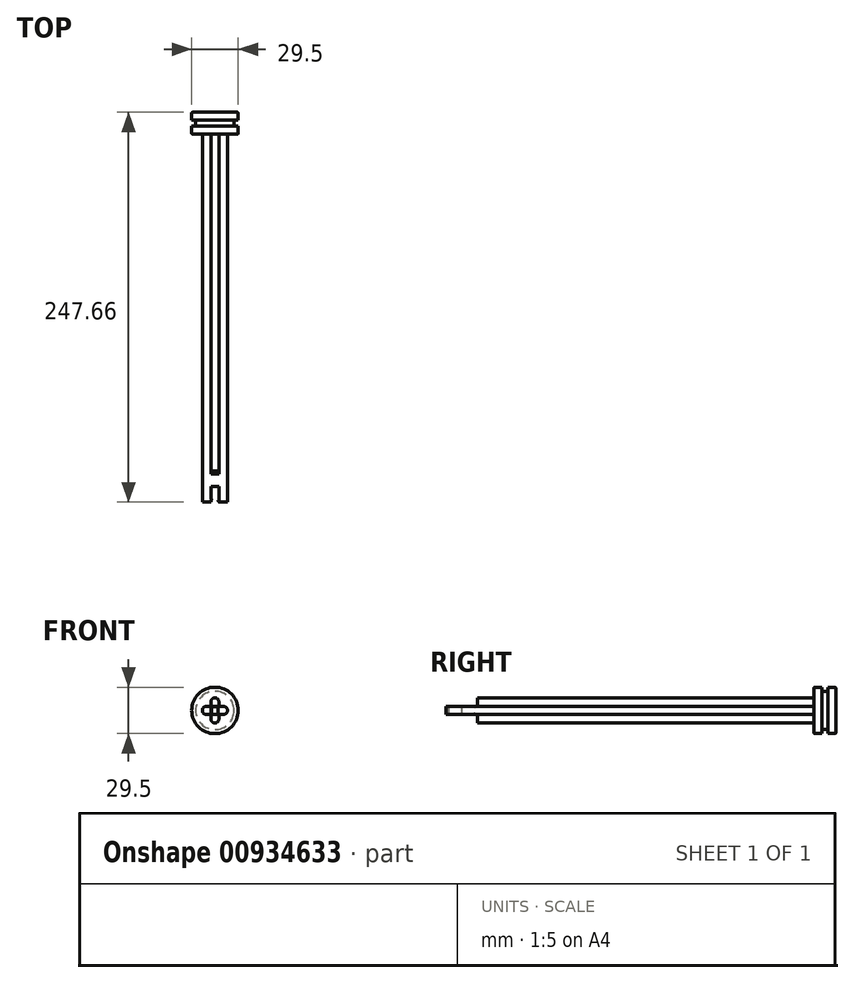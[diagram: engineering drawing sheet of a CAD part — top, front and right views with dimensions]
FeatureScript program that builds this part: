
annotation { "Feature Type Name" : "Feature", "Feature Type Description" : "" }
export const myFeature = defineFeature(function(context is Context, id is Id, definition is map)
    precondition{}
    {
        {
            var Q0;
            Q0=qCreatedBy(makeId("Front.planeOp"),FACE);
            var sketch = newSketch(context, id + "F0", { "sketchPlane" : qUnion([Q0])});
            skLineSegment(sketch, "E0.bottom", {"start": v(2.5, 8) * mm, "end": v(-2.5, 8) * mm});
            skLineSegment(sketch, "E0.top", {"start": v(2.5, -8) * mm, "end": v(-2.5, -8) * mm});
            skLineSegment(sketch, "E0.left", {"start": v(2.5, 8) * mm, "end": v(2.5, -8) * mm});
            skLineSegment(sketch, "E0.right", {"start": v(-2.5, 8) * mm, "end": v(-2.5, -8) * mm});
            skPoint(sketch, "E0.middle", {"position": v(0, 0) * mm});
            skLineSegment(sketch, "E1.bottom", {"start": v(-8, -2.5) * mm, "end": v(8, -2.5) * mm});
            skLineSegment(sketch, "E1.top", {"start": v(-8, 2.5) * mm, "end": v(8, 2.5) * mm});
            skLineSegment(sketch, "E1.left", {"start": v(-8, -2.5) * mm, "end": v(-8, 2.5) * mm});
            skLineSegment(sketch, "E1.right", {"start": v(8, -2.5) * mm, "end": v(8, 2.5) * mm});
            skSolve(sketch);
        }
        {
            var Q0;
            {var subQ5=sQuery(id+"F0.wireOp",EDGE,"E1.left");Q0=makeQuery(id+"F0.imprint","IMPRINT",FACE,{"disambiguationData":[TD([[makeQuery(id+"F0.imprint","IMPRINT",EDGE,{"derivedFrom":subQ5}),-1.0]])]});}
            var Q1;
            {var subQ0=sQuery(id+"F0.wireOp",EDGE,"E1.top");var subQ1=sQuery(id+"F0.wireOp",EDGE,"E0.left");var subQ2=makeQuery(id+"F0.imprint","INTERSECT",VERTEX,{"derivedFrom":[subQ1,subQ0]});Q1=makeQuery(id+"F0.imprint","IMPRINT",FACE,{"disambiguationData":[TD([[makeQuery(id+"F0.imprint","IMPRINT",EDGE,{"disambiguationData":[TD([[subQ2,-1.0]])],"derivedFrom":subQ1}),-1.0]])]});}
            var Q2;
            {var subQ5=sQuery(id+"F0.wireOp",EDGE,"E1.right");Q2=makeQuery(id+"F0.imprint","IMPRINT",FACE,{"disambiguationData":[TD([[makeQuery(id+"F0.imprint","IMPRINT",EDGE,{"derivedFrom":subQ5}),1.0]])]});}
            var Q3;
            {var subQ0=sQuery(id+"F0.wireOp",EDGE,"E0.top");Q3=makeQuery(id+"F0.imprint","IMPRINT",FACE,{"disambiguationData":[TD([[makeQuery(id+"F0.imprint","IMPRINT",EDGE,{"derivedFrom":subQ0}),-1.0]])]});}
            var Q4;
            {var subQ0=sQuery(id+"F0.wireOp",EDGE,"E0.bottom");Q4=makeQuery(id+"F0.imprint","IMPRINT",FACE,{"disambiguationData":[TD([[makeQuery(id+"F0.imprint","IMPRINT",EDGE,{"derivedFrom":subQ0}),1.0]])]});}
            extrude(context, id + "F1", {"entities" : qUnion([Q0, Q1, Q2, Q3, Q4]), "depth" : 233.86 * mm, "offsetDistance" : 25.4 * mm});
        }
        {
            var Q0;
            Q0=makeQuery(id+"F1.opExtrude","SWEPT_EDGE",EDGE,{"disambiguationData":[OSD([sQuery(id+"F0.wireOp",EDGE,"E0.bottom"),sQuery(id+"F0.wireOp",EDGE,"E0.right")])]});
            var Q1;
            Q1=makeQuery(id+"F1.opExtrude","SWEPT_EDGE",EDGE,{"disambiguationData":[OSD([sQuery(id+"F0.wireOp",EDGE,"E0.bottom"),sQuery(id+"F0.wireOp",EDGE,"E0.left")])]});
            var Q2;
            Q2=makeQuery(id+"F1.opExtrude","SWEPT_EDGE",EDGE,{"disambiguationData":[OSD([sQuery(id+"F0.wireOp",EDGE,"E1.top"),sQuery(id+"F0.wireOp",EDGE,"E1.left")])]});
            var Q3;
            Q3=makeQuery(id+"F1.opExtrude","SWEPT_EDGE",EDGE,{"disambiguationData":[OSD([sQuery(id+"F0.wireOp",EDGE,"E1.bottom"),sQuery(id+"F0.wireOp",EDGE,"E1.left")])]});
            var Q4;
            Q4=makeQuery(id+"F1.opExtrude","SWEPT_EDGE",EDGE,{"disambiguationData":[OSD([sQuery(id+"F0.wireOp",EDGE,"E0.top"),sQuery(id+"F0.wireOp",EDGE,"E0.right")])]});
            var Q5;
            Q5=makeQuery(id+"F1.opExtrude","SWEPT_EDGE",EDGE,{"disambiguationData":[OSD([sQuery(id+"F0.wireOp",EDGE,"E0.top"),sQuery(id+"F0.wireOp",EDGE,"E0.left")])]});
            var Q6;
            Q6=makeQuery(id+"F1.opExtrude","SWEPT_EDGE",EDGE,{"disambiguationData":[OSD([sQuery(id+"F0.wireOp",EDGE,"E1.bottom"),sQuery(id+"F0.wireOp",EDGE,"E1.right")])]});
            var Q7;
            Q7=makeQuery(id+"F1.opExtrude","SWEPT_EDGE",EDGE,{"disambiguationData":[OSD([sQuery(id+"F0.wireOp",EDGE,"E1.top"),sQuery(id+"F0.wireOp",EDGE,"E1.right")])]});
            fillet(context, id + "F2", {"entities" : qUnion([Q0, Q1, Q2, Q3, Q4, Q5, Q6, Q7]), "radius" : 2.5 * mm, "tangentPropagation" : true, "allowEdgeOverflow" : false});
        }
        {
            var Q0;
            Q0=qCreatedBy(makeId("Front.planeOp"),FACE);
            var sketch = newSketch(context, id + "F3", { "sketchPlane" : qUnion([Q0])});
            skCircle(sketch, "E2", {"center": v(0, 0) * mm, "radius": 14.75 * mm});
            skCircle(sketch, "E3", {"center": v(0, 0) * mm, "radius": 12.2 * mm});
            skSolve(sketch);
        }
        {
            var Q0;
            Q0=makeQuery(id+"F3.imprint","IMPRINT",FACE,{"disambiguationData":[TD([[makeQuery(id+"F3.imprint","IMPRINT",EDGE,{"derivedFrom":sQuery(id+"F3.wireOp",EDGE,"E2")}),1.0]])]});
            var Q1;
            Q1=makeQuery(id+"F3.imprint","IMPRINT",FACE,{"disambiguationData":[TD([[makeQuery(id+"F3.imprint","IMPRINT",EDGE,{"derivedFrom":sQuery(id+"F3.wireOp",EDGE,"E3")}),1.0]])]});
            extrude(context, id + "F4", {"entities" : qUnion([Q0, Q1]), "operationType" : NewBodyOperationType.ADD, "oppositeDirection" : true, "depth" : 13.8 * mm, "offsetDistance" : 25.4 * mm});
        }
        {
            var Q0;
            {var subQ0=sQuery(id+"F0.wireOp",EDGE,"E0.right");Q0=makeQuery(id+"F1.opExtrude","CAP_EDGE",EDGE,{"disambiguationData":[OSD([subQ0]),TDD([makeQuery(id+"F0.imprint","IMPRINT",EDGE,{"disambiguationData":[TD([[makeQuery(id+"F0.imprint","INTERSECT",VERTEX,{"derivedFrom":[sQuery(id+"F0.wireOp",EDGE,"E0.bottom"),subQ0]}),-1.0]])],"derivedFrom":subQ0})])],"isStart":true});}
            var Q1;
            Q1=makeQuery(id+"F4.opExtrude","CAP_FACE",FACE,{"disambiguationData":[OSD([sQuery(id+"F3.wireOp",EDGE,"E2")])],"isStart":true});
            var Q2;
            Q2=makeQuery(id+"F4.opExtrude","CAP_EDGE",EDGE,{"disambiguationData":[OSD([sQuery(id+"F3.wireOp",EDGE,"E2")])],"isStart":false});
            fillet(context, id + "F5", {"entities" : qUnion([Q0, Q1, Q2]), "radius" : 0.5 * mm, "tangentPropagation" : true, "allowEdgeOverflow" : false});
        }
        {
            var Q0;
            Q0=qCreatedBy(makeId("Right.planeOp"),FACE);
            var sketch = newSketch(context, id + "F6", { "sketchPlane" : qUnion([Q0])});
            skLineSegment(sketch, "E4.bottom", {"start": v(5, 22.2) * mm, "end": v(8.8, 22.2) * mm});
            skLineSegment(sketch, "E4.top", {"start": v(5, 12.2) * mm, "end": v(8.8, 12.2) * mm});
            skLineSegment(sketch, "E4.left", {"start": v(5, 22.2) * mm, "end": v(5, 12.2) * mm});
            skLineSegment(sketch, "E4.right", {"start": v(8.8, 22.2) * mm, "end": v(8.8, 12.2) * mm});
            skLineSegment(sketch, "E5", {"start": v(0, 0) * mm, "end": v(33.95, 0) * mm});
            skSolve(sketch);
        }
        {
            var Q0;
            Q0=makeQuery(id+"F6.imprint","IMPRINT",FACE,{"disambiguationData":[TD([[makeQuery(id+"F6.imprint","IMPRINT",EDGE,{"derivedFrom":sQuery(id+"F6.wireOp",EDGE,"E4.bottom")}),-1.0]])]});
            var Q1;
            Q1=sQuery(id+"F6.wireOp",EDGE,"E5");
            revolve(context, id + "F7", {"operationType" : NewBodyOperationType.REMOVE, "surfaceOperationType" : NewSurfaceOperationType.NEW, "entities" : qUnion([Q0]), "axis" : qUnion([Q1]), "revolveType" : RevolveType.FULL, "oppositeDirection" : true});
        }
        {
            var Q0;
            Q0=makeQuery(id+"F1.opExtrude","CAP_FACE",FACE,{"disambiguationData":[OSD([sQuery(id+"F0.wireOp",EDGE,"E0.bottom"),sQuery(id+"F0.wireOp",EDGE,"E0.top"),sQuery(id+"F0.wireOp",EDGE,"E0.left"),sQuery(id+"F0.wireOp",EDGE,"E0.right"),sQuery(id+"F0.wireOp",EDGE,"E1.bottom"),sQuery(id+"F0.wireOp",EDGE,"E1.top"),sQuery(id+"F0.wireOp",EDGE,"E1.left"),sQuery(id+"F0.wireOp",EDGE,"E1.right")])],"isStart":false});
            var sketch = newSketch(context, id + "F8", { "sketchPlane" : qUnion([Q0])});
            skLineSegment(sketch, "E6.bottom", {"start": v(2.5, 10) * mm, "end": v(-2.5, 10) * mm});
            skLineSegment(sketch, "E6.top", {"start": v(2.5, -10) * mm, "end": v(-2.5, -10) * mm});
            skLineSegment(sketch, "E6.left", {"start": v(2.5, 10) * mm, "end": v(2.5, -10) * mm});
            skLineSegment(sketch, "E6.right", {"start": v(-2.5, 10) * mm, "end": v(-2.5, -10) * mm});
            skPoint(sketch, "E6.middle", {"position": v(0, 0) * mm});
            skSolve(sketch);
        }
        {
            var Q0;
            {var subQ1=sQuery(id+"F0.wireOp",EDGE,"E1.top");var subQ2=sQuery(id+"F0.wireOp",EDGE,"E1.bottom");var subQ3=sQuery(id+"F0.wireOp",EDGE,"E0.right");var subQ4=sQuery(id+"F0.wireOp",EDGE,"E0.left");var subQ5=sQuery(id+"F0.wireOp",EDGE,"E0.top");var subQ6=sQuery(id+"F0.wireOp",EDGE,"E0.bottom");var subQ7=makeQuery(id+"F1.opExtrude","CAP_FACE",FACE,{"disambiguationData":[OSD([subQ6,subQ5,subQ4,subQ3,subQ2,subQ1,sQuery(id+"F0.wireOp",EDGE,"E1.left"),sQuery(id+"F0.wireOp",EDGE,"E1.right")])],"isStart":false});var subQ11=makeQuery(id+"F2.opFillet","BLEND_EDGE",EDGE,{"blendedFrom":[makeQuery(id+"F1.opExtrude","SWEPT_EDGE",EDGE,{"disambiguationData":[OSD([subQ6,subQ4])]}),subQ7],"blendedInto":[subQ7]});Q0=makeQuery(id+"F8.imprint","IMPRINT",FACE,{"disambiguationData":[TD([[makeQuery(id+"F8.imprint","IMPRINT",EDGE,{"derivedFrom":subQ11}),1.0]])]});}
            extrude(context, id + "F9", {"entities" : qUnion([Q0]), "operationType" : NewBodyOperationType.REMOVE, "oppositeDirection" : true, "depth" : 10 * mm, "offsetDistance" : 25 * mm});
        }
        {
            var Q0;
            Q0=makeQuery(id+"F9.boolean.opBoolean","COPY",FACE,{"derivedFrom":makeQuery(id+"F9.opExtrude","CAP_FACE",FACE,{"disambiguationData":[OSD([sQuery(id+"F0.wireOp",EDGE,"E0.bottom"),sQuery(id+"F0.wireOp",EDGE,"E0.top"),sQuery(id+"F0.wireOp",EDGE,"E0.left"),sQuery(id+"F0.wireOp",EDGE,"E0.right"),sQuery(id+"F0.wireOp",EDGE,"E1.bottom"),sQuery(id+"F0.wireOp",EDGE,"E1.top"),sQuery(id+"F0.wireOp",EDGE,"E1.left"),sQuery(id+"F0.wireOp",EDGE,"E1.right"),sQuery(id+"F8.wireOp",EDGE,"E6.left"),sQuery(id+"F8.wireOp",EDGE,"E6.right")])],"isStart":false})});
            var sketch = newSketch(context, id + "F10", { "sketchPlane" : qUnion([Q0])});
            skLineSegment(sketch, "E7.bottom", {"start": v(0, 8) * mm, "end": v(2.5, 8) * mm});
            skLineSegment(sketch, "E7.top", {"start": v(0, 2.5) * mm, "end": v(2.5, 2.5) * mm});
            skLineSegment(sketch, "E7.left", {"start": v(0, 8) * mm, "end": v(0, 2.5) * mm});
            skLineSegment(sketch, "E7.right", {"start": v(2.5, 8) * mm, "end": v(2.5, 2.5) * mm});
            skLineSegment(sketch, "E8.MirrorCS", {"start": v(0, 8) * mm, "end": v(-2.5, 8) * mm});
            skLineSegment(sketch, "E9.MirrorCS", {"start": v(-2.5, 8) * mm, "end": v(-2.5, 2.5) * mm});
            skLineSegment(sketch, "E10.MirrorCS", {"start": v(0, 2.5) * mm, "end": v(-2.5, 2.5) * mm});
            skLineSegment(sketch, "E11.bottom", {"start": v(-2.5, 8) * mm, "end": v(2.5, 8) * mm});
            skLineSegment(sketch, "E11.top", {"start": v(-2.5, 2.5) * mm, "end": v(2.5, 2.5) * mm});
            skLineSegment(sketch, "E12.MirrorCS", {"start": v(-2.5, -8) * mm, "end": v(-2.5, -2.5) * mm});
            skLineSegment(sketch, "E13.MirrorCS", {"start": v(-2.5, -8) * mm, "end": v(2.5, -8) * mm});
            skLineSegment(sketch, "E14.MirrorCS", {"start": v(2.5, -8) * mm, "end": v(2.5, -2.5) * mm});
            skLineSegment(sketch, "E15.MirrorCS", {"start": v(-2.5, -2.5) * mm, "end": v(2.5, -2.5) * mm});
            skSolve(sketch);
        }
        {
            var Q0;
            {var subQ15=sQuery(id+"F10.wireOp",EDGE,"E7.left");Q0=makeQuery(id+"F10.imprint","IMPRINT",FACE,{"disambiguationData":[TD([[makeQuery(id+"F10.imprint","IMPRINT",EDGE,{"derivedFrom":subQ15}),-1.0]])]});}
            var Q1;
            {var subQ13=sQuery(id+"F10.wireOp",EDGE,"E7.left");Q1=makeQuery(id+"F10.imprint","IMPRINT",FACE,{"disambiguationData":[TD([[makeQuery(id+"F10.imprint","IMPRINT",EDGE,{"derivedFrom":subQ13}),1.0]])]});}
            var Q2;
            {var subQ16=sQuery(id+"F10.wireOp",EDGE,"E15.MirrorCS");Q2=makeQuery(id+"F10.imprint","IMPRINT",FACE,{"disambiguationData":[TD([[makeQuery(id+"F10.imprint","IMPRINT",EDGE,{"derivedFrom":subQ16}),-1.0]])]});}
            extrude(context, id + "F11", {"entities" : qUnion([Q0, Q1, Q2]), "operationType" : NewBodyOperationType.REMOVE, "oppositeDirection" : true, "depth" : 10 * mm, "offsetDistance" : 25 * mm});
        }
        {
            var Q0;
            {var subQ0=sQuery(id+"F0.wireOp",EDGE,"E1.top");Q0=makeQuery(id+"F11.boolean.opBoolean","MERGE",FACE,{"derivedFrom":[makeQuery(id+"F1.opExtrude","SWEPT_FACE",FACE,{"disambiguationData":[OSD([subQ0]),TDD([makeQuery(id+"F0.imprint","IMPRINT",EDGE,{"disambiguationData":[TD([[makeQuery(id+"F0.imprint","INTERSECT",VERTEX,{"derivedFrom":[subQ0,sQuery(id+"F0.wireOp",EDGE,"E1.left")]}),-1.0]])],"derivedFrom":subQ0})])]}),makeQuery(id+"F1.opExtrude","SWEPT_FACE",FACE,{"disambiguationData":[OSD([subQ0]),TDD([makeQuery(id+"F0.imprint","IMPRINT",EDGE,{"disambiguationData":[TD([[makeQuery(id+"F0.imprint","INTERSECT",VERTEX,{"derivedFrom":[subQ0,sQuery(id+"F0.wireOp",EDGE,"E1.right")]}),1.0]])],"derivedFrom":subQ0})])]})],"fromTools":[makeQuery(id+"F11.opExtrude","SWEPT_FACE",FACE,{"disambiguationData":[OSD([sQuery(id+"F10.wireOp",EDGE,"E11.top")])]})]});}
            var sketch = newSketch(context, id + "F12", { "sketchPlane" : qUnion([Q0])});
            skLineSegment(sketch, "E16", {"start": v(2.5, -233.86) * mm, "end": v(2, -232.36) * mm});
            skLineSegment(sketch, "E17", {"start": v(2, -232.36) * mm, "end": v(2.5, -232.36) * mm});
            skLineSegment(sketch, "E18.bottom", {"start": v(2.5, -232.36) * mm, "end": v(2, -232.36) * mm});
            skLineSegment(sketch, "E18.top", {"start": v(2.5, -231.86) * mm, "end": v(2, -231.86) * mm});
            skLineSegment(sketch, "E18.left", {"start": v(2.5, -232.36) * mm, "end": v(2.5, -231.86) * mm});
            skLineSegment(sketch, "E18.right", {"start": v(2, -232.36) * mm, "end": v(2, -231.86) * mm});
            skLineSegment(sketch, "E19.bottom", {"start": v(-2.5, -233.86) * mm, "end": v(2.5, -233.86) * mm, "construction": true});
            skLineSegment(sketch, "E19.top", {"start": v(-2.5, -221.37) * mm, "end": v(2.5, -221.37) * mm, "construction": true});
            skLineSegment(sketch, "E19.left", {"start": v(-2.5, -233.86) * mm, "end": v(-2.5, -221.37) * mm, "construction": true});
            skLineSegment(sketch, "E19.right", {"start": v(2.5, -233.86) * mm, "end": v(2.5, -221.37) * mm, "construction": true});
            skLineSegment(sketch, "E20", {"start": v(0, -224.68) * mm, "end": v(0, -221.37) * mm, "construction": true});
            skPoint(sketch, "E20.startSnap0", {"position": v(0, -221.37) * mm});
            skLineSegment(sketch, "E21.MirrorCS", {"start": v(-2, -232.36) * mm, "end": v(-2.5, -232.36) * mm});
            skLineSegment(sketch, "E22.MirrorCS", {"start": v(-2.5, -232.36) * mm, "end": v(-2.5, -231.86) * mm});
            skLineSegment(sketch, "E23.MirrorCS", {"start": v(-2.5, -232.36) * mm, "end": v(-2, -232.36) * mm});
            skLineSegment(sketch, "E24.MirrorCS", {"start": v(-2, -232.36) * mm, "end": v(-2, -231.86) * mm});
            skLineSegment(sketch, "E25.MirrorCS", {"start": v(-2.5, -233.86) * mm, "end": v(-2, -232.36) * mm});
            skLineSegment(sketch, "E26.MirrorCS", {"start": v(-2.5, -231.86) * mm, "end": v(-2, -231.86) * mm});
            skSolve(sketch);
        }
        {
            var Q0;
            Q0=makeQuery(id+"F12.imprint","IMPRINT",FACE,{"disambiguationData":[TD([[makeQuery(id+"F12.imprint","IMPRINT",EDGE,{"derivedFrom":sQuery(id+"F12.wireOp",EDGE,"E22.MirrorCS")}),-1.0]])]});
            var Q1;
            {var subQ0=sQuery(id+"F12.wireOp",EDGE,"E23.MirrorCS");Q1=makeQuery(id+"F12.imprint","IMPRINT",FACE,{"disambiguationData":[TD([[makeQuery(id+"F12.imprint","IMPRINT",EDGE,{"derivedFrom":subQ0}),-1.0]])]});}
            var Q2;
            Q2=makeQuery(id+"F12.imprint","IMPRINT",FACE,{"disambiguationData":[TD([[makeQuery(id+"F12.imprint","IMPRINT",EDGE,{"derivedFrom":sQuery(id+"F12.wireOp",EDGE,"E18.bottom")}),-1.0]])]});
            var Q3;
            {var subQ0=sQuery(id+"F12.wireOp",EDGE,"E16");Q3=makeQuery(id+"F12.imprint","IMPRINT",FACE,{"disambiguationData":[TD([[makeQuery(id+"F12.imprint","IMPRINT",EDGE,{"derivedFrom":subQ0}),-1.0]])]});}
            extrude(context, id + "F13", {"entities" : qUnion([Q0, Q1, Q2, Q3]), "operationType" : NewBodyOperationType.ADD, "oppositeDirection" : true, "depth" : 5 * mm, "offsetDistance" : 25 * mm});
        }
        {
            var Q0;
            Q0=makeQuery(id+"F13.boolean.opBoolean","MERGE",EDGE,{"derivedFrom":[makeQuery(id+"F9.boolean.opBoolean","COPY",EDGE,{"derivedFrom":makeQuery(id+"F9.opExtrude","CAP_EDGE",EDGE,{"disambiguationData":[OSD([sQuery(id+"F8.wireOp",EDGE,"E6.right")])],"isStart":true})}),makeQuery(id+"F13.opExtrude","SWEPT_EDGE",EDGE,{"disambiguationData":[OSD([sQuery(id+"F0.wireOp",EDGE,"E0.right"),sQuery(id+"F0.wireOp",EDGE,"E1.top"),sQuery(id+"F12.wireOp",EDGE,"E25.MirrorCS")])]})]});
            var Q1;
            Q1=makeQuery(id+"F13.boolean.opBoolean","MERGE",EDGE,{"derivedFrom":[makeQuery(id+"F9.boolean.opBoolean","COPY",EDGE,{"derivedFrom":makeQuery(id+"F9.opExtrude","CAP_EDGE",EDGE,{"disambiguationData":[OSD([sQuery(id+"F8.wireOp",EDGE,"E6.left")])],"isStart":true})}),makeQuery(id+"F13.opExtrude","SWEPT_EDGE",EDGE,{"disambiguationData":[OSD([sQuery(id+"F0.wireOp",EDGE,"E0.left"),sQuery(id+"F0.wireOp",EDGE,"E1.top"),sQuery(id+"F12.wireOp",EDGE,"E16")])]})]});
            fillet(context, id + "F14", {"entities" : qUnion([Q0, Q1]), "radius" : .5 * mm, "tangentPropagation" : true, "allowEdgeOverflow" : false});
        }
        {
            var Q0;
            {var subQ0=sQuery(id+"F0.wireOp",EDGE,"E0.left");Q0=makeQuery(id+"F1.opExtrude","SWEPT_FACE",FACE,{"disambiguationData":[OSD([subQ0]),TDD([makeQuery(id+"F0.imprint","IMPRINT",EDGE,{"disambiguationData":[TD([[makeQuery(id+"F0.imprint","INTERSECT",VERTEX,{"derivedFrom":[sQuery(id+"F0.wireOp",EDGE,"E0.bottom"),subQ0]}),-1.0]])],"derivedFrom":subQ0})])]});}
            var sketch = newSketch(context, id + "F15", { "sketchPlane" : qUnion([Q0])});
            skLineSegment(sketch, "E27", {"start": v(-213.86, 2.5) * mm, "end": v(-213.86, -2.5) * mm, "construction": true});
            skPoint(sketch, "E28", {"position": v(-213.86, 0) * mm});
            skLineSegment(sketch, "E29", {"start": v(-213.86, 2.5) * mm, "end": v(-215.4, 2.5) * mm});
            skLineSegment(sketch, "E30", {"start": v(-215.4, 2.5) * mm, "end": v(-215.4, 2) * mm});
            skLineSegment(sketch, "E31", {"start": v(-215.4, 2) * mm, "end": v(-213.86, 2.5) * mm});
            skLineSegment(sketch, "E32.bottom", {"start": v(-215.4, 2.5) * mm, "end": v(-215.9, 2.5) * mm});
            skLineSegment(sketch, "E32.top", {"start": v(-215.4, 2) * mm, "end": v(-215.9, 2) * mm});
            skLineSegment(sketch, "E32.right", {"start": v(-215.9, 2.5) * mm, "end": v(-215.9, 2) * mm});
            skLineSegment(sketch, "E33", {"start": v(-208.07, 0) * mm, "end": v(-213.86, 0) * mm, "construction": true});
            skLineSegment(sketch, "E34.MirrorCS", {"start": v(-215.4, -2.5) * mm, "end": v(-215.4, -2) * mm});
            skLineSegment(sketch, "E35.MirrorCS", {"start": v(-215.9, -2.5) * mm, "end": v(-215.9, -2) * mm});
            skLineSegment(sketch, "E36.MirrorCS", {"start": v(-215.4, -2.5) * mm, "end": v(-215.9, -2.5) * mm});
            skLineSegment(sketch, "E37.MirrorCS", {"start": v(-215.4, -2) * mm, "end": v(-213.86, -2.5) * mm});
            skLineSegment(sketch, "E38.MirrorCS", {"start": v(-213.86, -2.5) * mm, "end": v(-215.4, -2.5) * mm});
            skLineSegment(sketch, "E39.MirrorCS", {"start": v(-215.4, -2) * mm, "end": v(-215.9, -2) * mm});
            skSolve(sketch);
        }
        {
            var Q0;
            Q0 = qSketchRegion(id + "F15", true);
            extrude(context, id + "F16", {"entities" : qUnion([Q0]), "operationType" : NewBodyOperationType.REMOVE, "oppositeDirection" : true, "depth" : 5 * mm, "offsetDistance" : 25 * mm});
        }
        {
            var Q0;
            Q0=makeQuery(id+"F7.boolean.opBoolean","COPY",EDGE,{"derivedFrom":makeQuery(id+"F7.opRevolve","SWEPT_EDGE",EDGE,{"disambiguationData":[OSD([sQuery(id+"F6.wireOp",EDGE,"E4.top"),sQuery(id+"F6.wireOp",EDGE,"E4.right")])]})});
            var Q1;
            Q1=makeQuery(id+"F7.boolean.opBoolean","COPY",EDGE,{"derivedFrom":makeQuery(id+"F7.opRevolve","SWEPT_EDGE",EDGE,{"disambiguationData":[OSD([sQuery(id+"F6.wireOp",EDGE,"E4.top"),sQuery(id+"F6.wireOp",EDGE,"E4.left")])]})});
            fillet(context, id + "F17", {"entities" : qUnion([Q0, Q1]), "radius" : 1 * mm, "tangentPropagation" : true, "allowEdgeOverflow" : false});
        }
    });
